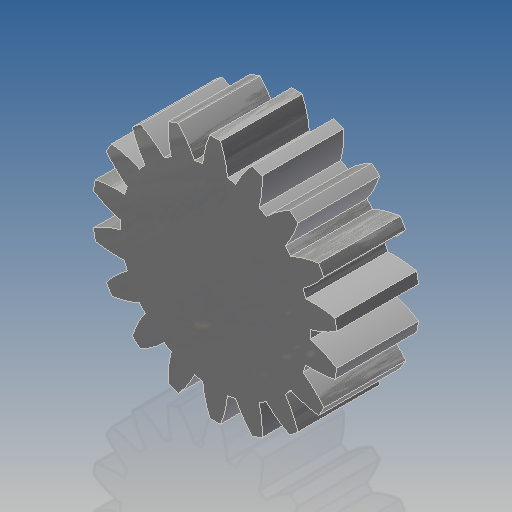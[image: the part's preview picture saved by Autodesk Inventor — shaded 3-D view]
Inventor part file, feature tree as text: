
AUTODESK INVENTOR PART (.ipt)
format: ipt  version: 2017 (Build 210142000, 142)  size: 261,120 bytes
history: native  units: mm (DEFAULTED — no unit token found)
features: plane x3, other x3, sketch x2, extrude x1
ambient origin geometry x8: Origin, YZ Plane, XZ Plane, XY Plane, X Axis, Y Axis, Z Axis, Center Point
bodies: Solid1 (feature_tree)
feature tree (9):
  extrude  "Extrusion1"  Depth=10.0mm TaperAngle=0.0deg
  plane  "Work Plane2"
  plane  "Work Plane8"
  plane  "Work Plane9"
  other  "Engranaje recto"
  sketch  "Sketch1"  dims[d0=30.0mm d1=10.0mm d2=0.0mm]
  sketch  "Sketch2"  dims[d3=27.0mm d4=10.0mm d5=0.0mm d16=67.5mm d17=0.0mm d34=1.745329mm d39=0.0mm d41=0.0mm d43=67.5mm d46=67.5mm d47=0.0mm d48=0.0mm]
  other  "Srf1"
  other  "Diámetro de separación"
